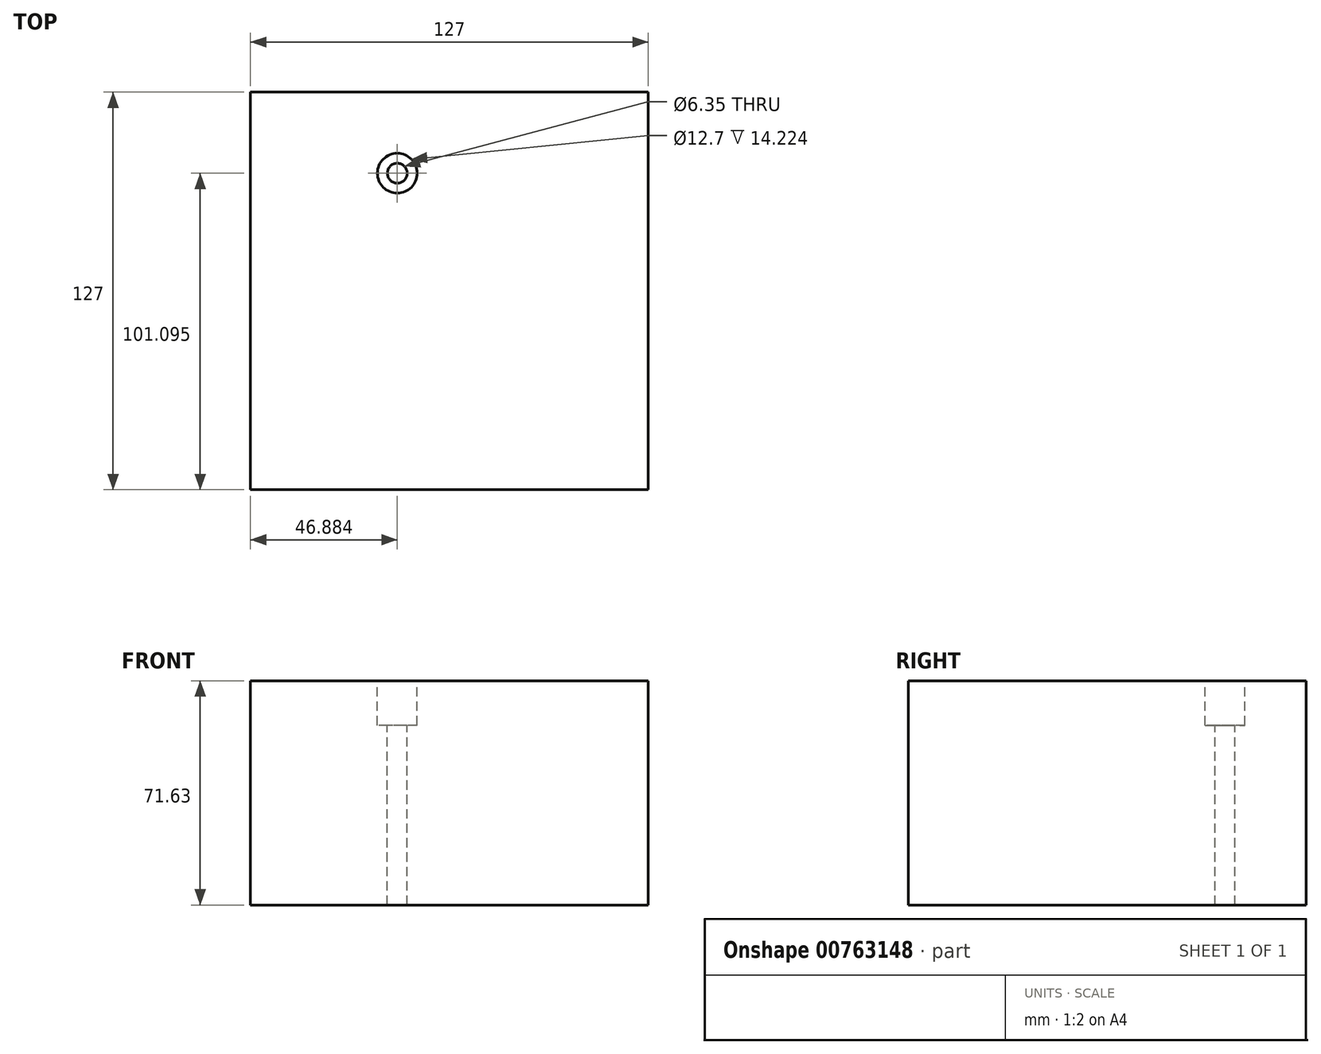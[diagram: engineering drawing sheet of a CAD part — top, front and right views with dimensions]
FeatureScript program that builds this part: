
annotation { "Feature Type Name" : "Feature", "Feature Type Description" : "" }
export const myFeature = defineFeature(function(context is Context, id is Id, definition is map)
    precondition{}
    {
        {
            var Q0;
            Q0=qCreatedBy(makeId("Front.planeOp"),FACE);
            var sketch = newSketch(context, id + "F0", { "sketchPlane" : qUnion([Q0])});
            skLineSegment(sketch, "E0.bottom", {"start": v(-59.84, 38.6) * mm, "end": v(67.16, 38.6) * mm});
            skLineSegment(sketch, "E0.top", {"start": v(-59.84, -33.04) * mm, "end": v(67.16, -33.04) * mm});
            skLineSegment(sketch, "E0.left", {"start": v(-59.84, 38.6) * mm, "end": v(-59.84, -33.04) * mm});
            skLineSegment(sketch, "E0.right", {"start": v(67.16, 38.6) * mm, "end": v(67.16, -33.04) * mm});
            skSolve(sketch);
        }
        {
            var Q0;
            Q0=makeQuery(id+"F0.imprint","IMPRINT",FACE,{"disambiguationData":[TD([[makeQuery(id+"F0.imprint","IMPRINT",EDGE,{"derivedFrom":sQuery(id+"F0.wireOp",EDGE,"E0.bottom")}),-1.0]])]});
            extrude(context, id + "F1", {"entities" : qUnion([Q0]), "depth" : 127 * mm, "offsetDistance" : 25.4 * mm});
        }
        {
            var Q0;
            Q0=makeQuery(id+"F1.opExtrude","SWEPT_FACE",FACE,{"disambiguationData":[OSD([sQuery(id+"F0.wireOp",EDGE,"E0.bottom")])]});
            var sketch = newSketch(context, id + "F2", { "sketchPlane" : qUnion([Q0])});
            skCircle(sketch, "E1", {"center": v(-12.96, -25.9) * mm, "radius": 18.37 * mm});
            skSolve(sketch);
        }
        {
            var Q0;
            Q0=sQuery(id+"F2.wireOp",VERTEX,"E1.center");
            var Q1;
            Q1=makeQuery(id+"F1.opExtrude","SWEPT_BODY",BODY,{"disambiguationData":[OSD([sQuery(id+"F0.wireOp",EDGE,"E0.bottom"),sQuery(id+"F0.wireOp",EDGE,"E0.top"),sQuery(id+"F0.wireOp",EDGE,"E0.left"),sQuery(id+"F0.wireOp",EDGE,"E0.right")])]});
            hole(context, id + "F3", {"style" : HoleStyle.C_BORE, "endStyle" : HoleEndStyle.THROUGH, "holeDiameter" : 6.35 * mm, "cBoreDiameter" : 12.7 * mm, "cBoreDepth" : 14.22 * mm, "majorDiameter" : 6.35 * mm, "isTappedThrough" : true, "tappedDepth" : 12.7 * mm, "tapClearance" : 3, "startFromSketch" : true, "locations" : qUnion([Q0]), "scope" : qUnion([Q1])});
        }
    });
